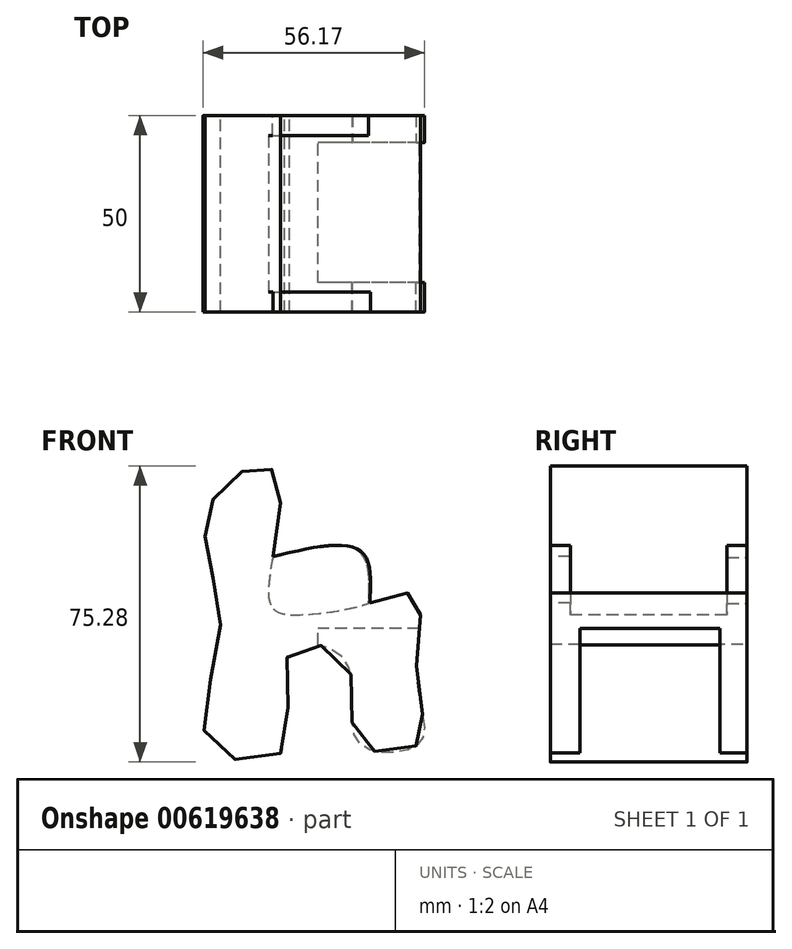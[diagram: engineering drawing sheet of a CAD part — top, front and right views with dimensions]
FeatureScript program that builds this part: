
annotation { "Feature Type Name" : "Feature", "Feature Type Description" : "" }
export const myFeature = defineFeature(function(context is Context, id is Id, definition is map)
    precondition{}
    {
        {
            var Q0;
            Q0=qCreatedBy(makeId("Front.planeOp"),FACE);
            var sketch = newSketch(context, id + "F0", { "sketchPlane" : qUnion([Q0])});
            skFitSpline(sketch, "E0", {"points": [v(-24.98, 13.2) * mm, v(-28.43, 35.81) * mm, v(-25.3, 50.58) * mm, v(-13.35, 56.86) * mm, v(-9.58, 46.18) * mm, v(-12.1, 21.68) * mm, v(-4.56, 19.16) * mm, v(12.72, 22) * mm, v(24.98, 23.88) * mm, v(24.98, 2.83) * mm, v(25.6, -13.5) * mm, v(10.21, -13.2) * mm, v(7.07, 7.23) * mm, v(-7.38, 9.42) * mm, v(-8.64, -15.08) * mm, v(-27.49, -13.82) * mm, v(-24.98, 13.2) * mm]});
            skSolve(sketch);
        }
        {
            var Q0;
            Q0 = qSketchRegion(id + "F0", true);
            extrude(context, id + "F1", {"entities" : qUnion([Q0]), "depth" : 50 * mm, "offsetDistance" : 25 * mm});
        }
        {
            var Q0;
            Q0=qCreatedBy(makeId("Right.planeOp"),FACE);
            var sketch = newSketch(context, id + "F2", { "sketchPlane" : qUnion([Q0])});
            skLineSegment(sketch, "E1.bottom", {"start": v(-42.39, -18.31) * mm, "end": v(-6.92, -18.31) * mm});
            skLineSegment(sketch, "E1.top", {"start": v(-42.39, 15.73) * mm, "end": v(-6.92, 15.73) * mm});
            skLineSegment(sketch, "E1.left", {"start": v(-42.39, -18.31) * mm, "end": v(-42.39, 15.73) * mm});
            skLineSegment(sketch, "E1.right", {"start": v(-6.92, -18.31) * mm, "end": v(-6.92, 15.73) * mm});
            skSolve(sketch);
        }
        {
            var Q0;
            Q0 = qSketchRegion(id + "F2", true);
            extrude(context, id + "F3", {"entities" : qUnion([Q0]), "operationType" : NewBodyOperationType.REMOVE, "endBound" : BoundingType.THROUGH_ALL, "depth" : 25 * mm, "offsetDistance" : 25 * mm});
        }
        {
            var Q0;
            Q0=makeQuery(id+"F1.opExtrude","CAP_FACE",FACE,{"disambiguationData":[OSD([sQuery(id+"F0.wireOp",EDGE,"E0")])],"isStart":false});
            var sketch = newSketch(context, id + "F4", { "sketchPlane" : qUnion([Q0])});
            skFitSpline(sketch, "E2", {"points": [v(-11.5, 33.96) * mm, v(10.8, 35.33) * mm, v(13.13, 22.12) * mm], "startDerivative": vector(49.12, 11.63) * mm, "endDerivative": vector(-2.14, -37.24) * mm});
            skSolve(sketch);
        }
        {
            var Q0;
            {var subQ0=sQuery(id+"F4.wireOp",EDGE,"E2");Q0=makeQuery(id+"F4.imprint","IMPRINT",FACE,{"disambiguationData":[TD([[makeQuery(id+"F4.imprint","IMPRINT",EDGE,{"derivedFrom":subQ0}),-1.0]])]});}
            extrude(context, id + "F5", {"entities" : qUnion([Q0]), "operationType" : NewBodyOperationType.ADD, "oppositeDirection" : true, "depth" : 5.1 * mm, "offsetDistance" : 25 * mm});
        }
        {
            var Q0;
            Q0=makeQuery(id+"F1.opExtrude","CAP_FACE",FACE,{"disambiguationData":[OSD([sQuery(id+"F0.wireOp",EDGE,"E0")])],"isStart":true});
            var sketch = newSketch(context, id + "F6", { "sketchPlane" : qUnion([Q0])});
            skFitSpline(sketch, "E3", {"points": [v(11.55, 33.73) * mm, v(-10.13, 35.45) * mm, v(-12.69, 21.98) * mm], "startDerivative": vector(-48.07, 12.38) * mm, "endDerivative": vector(1.57, -37.69) * mm});
            skSolve(sketch);
        }
        {
            var Q0;
            {var subQ0=sQuery(id+"F6.wireOp",EDGE,"E3");Q0=makeQuery(id+"F6.imprint","IMPRINT",FACE,{"disambiguationData":[TD([[makeQuery(id+"F6.imprint","IMPRINT",EDGE,{"derivedFrom":subQ0}),1.0]])]});}
            extrude(context, id + "F7", {"entities" : qUnion([Q0]), "operationType" : NewBodyOperationType.ADD, "oppositeDirection" : true, "depth" : 5.1 * mm, "offsetDistance" : 25 * mm});
        }
    });
